# Revit family: Desks-Teknion-LWBDH_Byward_Desk_with_Hinged_Door-R2022
name_source: partatom
category: Furniture
units: mm (PartAtom-declared; Revit-internal decimal feet)

## family parameters
Always vertical = Yes
Cut with Voids When Loaded = No
OmniClass Number = 23.40.20.00
OmniClass Title = General Furniture and Specialties
Render Appearance Source = Family Geometry
Room Calculation Point = No
Shared = Yes
Work Plane-Based = No

## types (5) — shared parameters
Assembly Code = E2020200
Manufacturer = Teknion
Manufacturer Fax = 416.661.4586
Metal Leg Finish = Paint-Teknion-23-Z-Foundation-Foundry Onyx
Metal Tab = 6.783 "
Model = LWBDP_____
Part Number = LWBDP
Product Documentation Link = https://assets.teknion.com
Product Line = Byward
Product Page URL = https://www.teknion.com
Series = Byward
Sustainability Data = https://www.teknion.com
URL = www.teknion.com
Unit Weight URL = http://www.teknion.com
Warranty = http://www.teknion.com
zero-valued in all types: Default Elevation

## per-type parameters (varying)
| type | Description |
| Byward Pull | Byward Desk with Hinged Door, Byward Pull Handle |
| Rectangular Pull | Byward Desk with Hinged Door, Rectangular Pull Handle |
| Journal Pull | Byward Desk with Hinged Door, Journal Pull Handle |
| Modern Straight (ADA) | Byward Desk with Hinged Door, Modern Straight (ADA) Handle |
| Byward Tab | Byward Desk with Pedestal, Byward Pull Handle |

type visibility flags: 5 boolean params named "<type name> Handle" — each type sets only its own to Yes (folded from table)

## geometry (parser evidence)
native form markers: Sweep x3
no freeform markers — native parametric forms only
